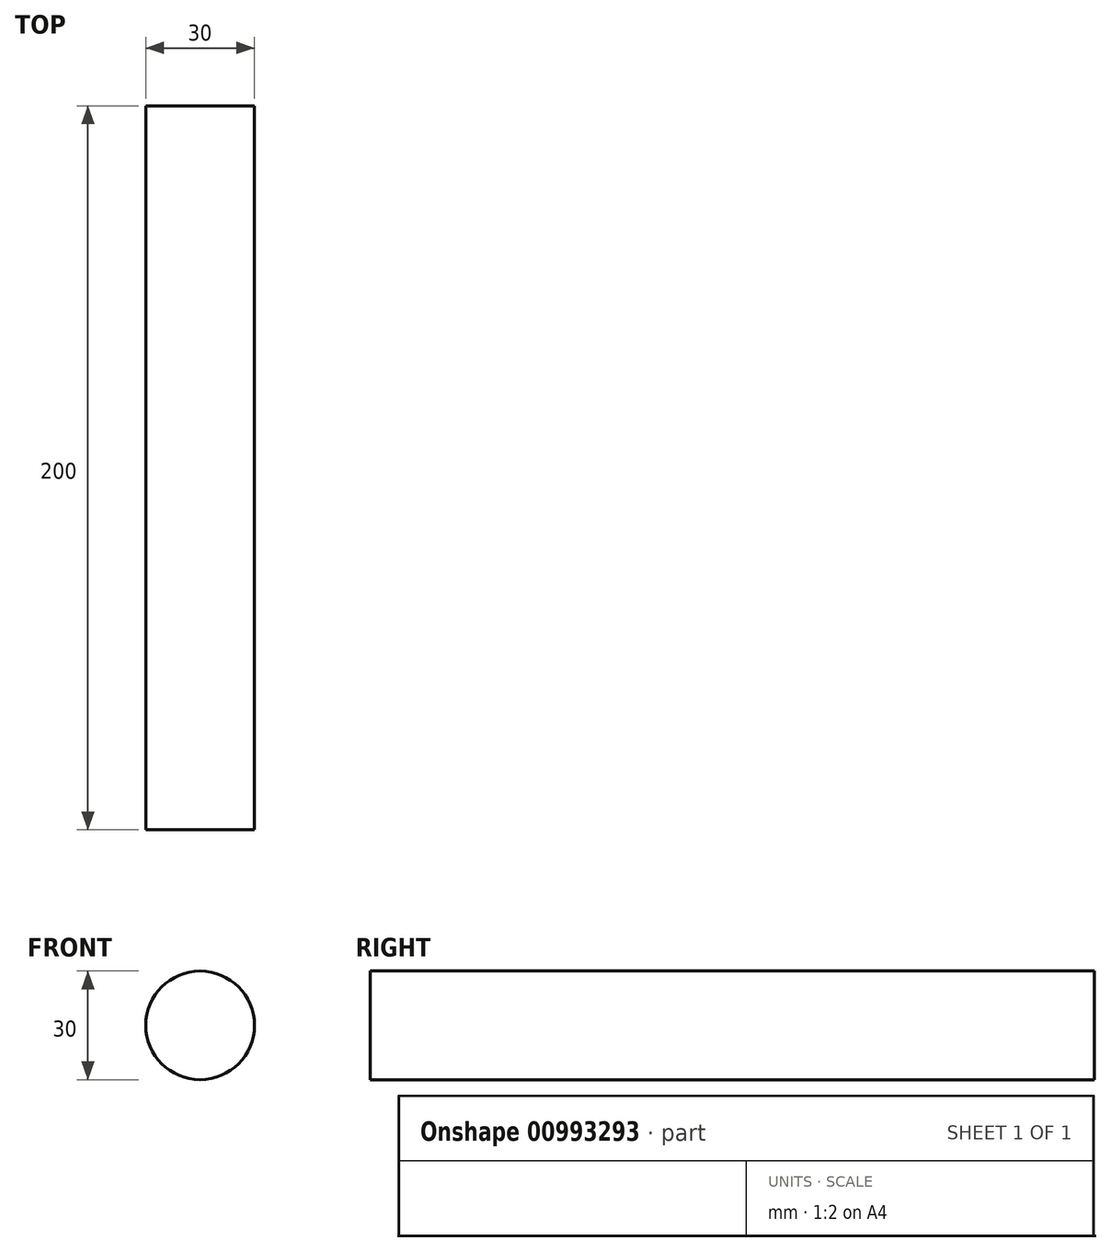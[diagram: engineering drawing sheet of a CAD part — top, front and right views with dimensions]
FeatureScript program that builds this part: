
annotation { "Feature Type Name" : "Feature", "Feature Type Description" : "" }
export const myFeature = defineFeature(function(context is Context, id is Id, definition is map)
    precondition{}
    {
        {
            var Q0;
            Q0=qCreatedBy(makeId("Top.planeOp"),FACE);
            var sketch = newSketch(context, id + "F0", { "sketchPlane" : qUnion([Q0])});
            skLineSegment(sketch, "E0.bottom", {"start": v(-15, 97.21) * mm, "end": v(15, 97.21) * mm});
            skLineSegment(sketch, "E0.top", {"start": v(-15, -102.79) * mm, "end": v(15, -102.79) * mm});
            skLineSegment(sketch, "E0.left", {"start": v(-15, 97.21) * mm, "end": v(-15, -102.79) * mm});
            skLineSegment(sketch, "E0.right", {"start": v(15, 97.21) * mm, "end": v(15, -102.79) * mm});
            skLineSegment(sketch, "E1", {"start": v(0, 97.21) * mm, "end": v(0, -102.79) * mm});
            skSolve(sketch);
        }
        {
            var Q0;
            {var subQ0=sQuery(id+"F0.wireOp",EDGE,"E0.right");Q0=makeQuery(id+"F0.imprint","IMPRINT",FACE,{"disambiguationData":[TD([[makeQuery(id+"F0.imprint","IMPRINT",EDGE,{"derivedFrom":subQ0}),-1.0]])]});}
            var Q1;
            Q1=sQuery(id+"F0.wireOp",EDGE,"E1");
            revolve(context, id + "F1", {"surfaceOperationType" : NewSurfaceOperationType.NEW, "entities" : qUnion([Q0]), "axis" : qUnion([Q1]), "revolveType" : RevolveType.FULL});
        }
    });
